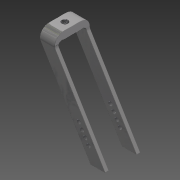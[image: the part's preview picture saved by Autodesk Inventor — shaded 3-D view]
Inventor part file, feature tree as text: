
AUTODESK INVENTOR PART (.ipt)
format: ipt  version: 2015 (Build 190159000, 159)  size: 660,480 bytes
history: native  units: mm
features: sketch x8, other x5, fillet x3, hole x2, sweep x1, loft x1, mirror x1, pattern_linear x1, projected_geometry x1
ambient origin geometry x8: Origin, YZ Plane, XZ Plane, XY Plane, X Axis, Y Axis, Z Axis, Center Point
bodies: Body1 (feature_tree)
feature tree (23):
  other  "Bryła1"
  sweep  "Przeciągnięcie1"
  other  "Płaszczyzna konstrukcyjna1"
  sketch  "Szkic3"
  sketch  "Szkic4"
  other  "Płaszczyzna konstrukcyjna2"
  sketch  "Szkic5"
  other  "Płaszczyzna konstrukcyjna3"
  loft  "Wyciągnięcie złożone1"
  mirror  "Odbicie lustrzane2"
  other  "Płaszczyzna konstrukcyjna4"
  hole  "Otwór1"  [1 undecoded]
  hole  "Otwór2"  [1 undecoded]
  pattern_linear  "Szyk prostokątny2"  Spacing1=0.0mm  [1 undecoded]
  fillet  "Zaokrąglenie4"  Radius=12.0mm
  fillet  "Zaokrąglenie5"  Radius=22.5mm
  fillet  "Zaokrąglenie6"  Radius=15.0mm
  sketch  "Szkic1"
  sketch  "Szkic2"
  projected_geometry  "Pętla rzutowana1"
  sketch  "Szkic6"
  sketch  "Szkic7"
  sketch  "Szkic8"
note: 3 required parameter values undecoded (feature->parameter linkage not recoverable at this tier; creation-order binding heuristic only, values carry confidence <= 0.55)
